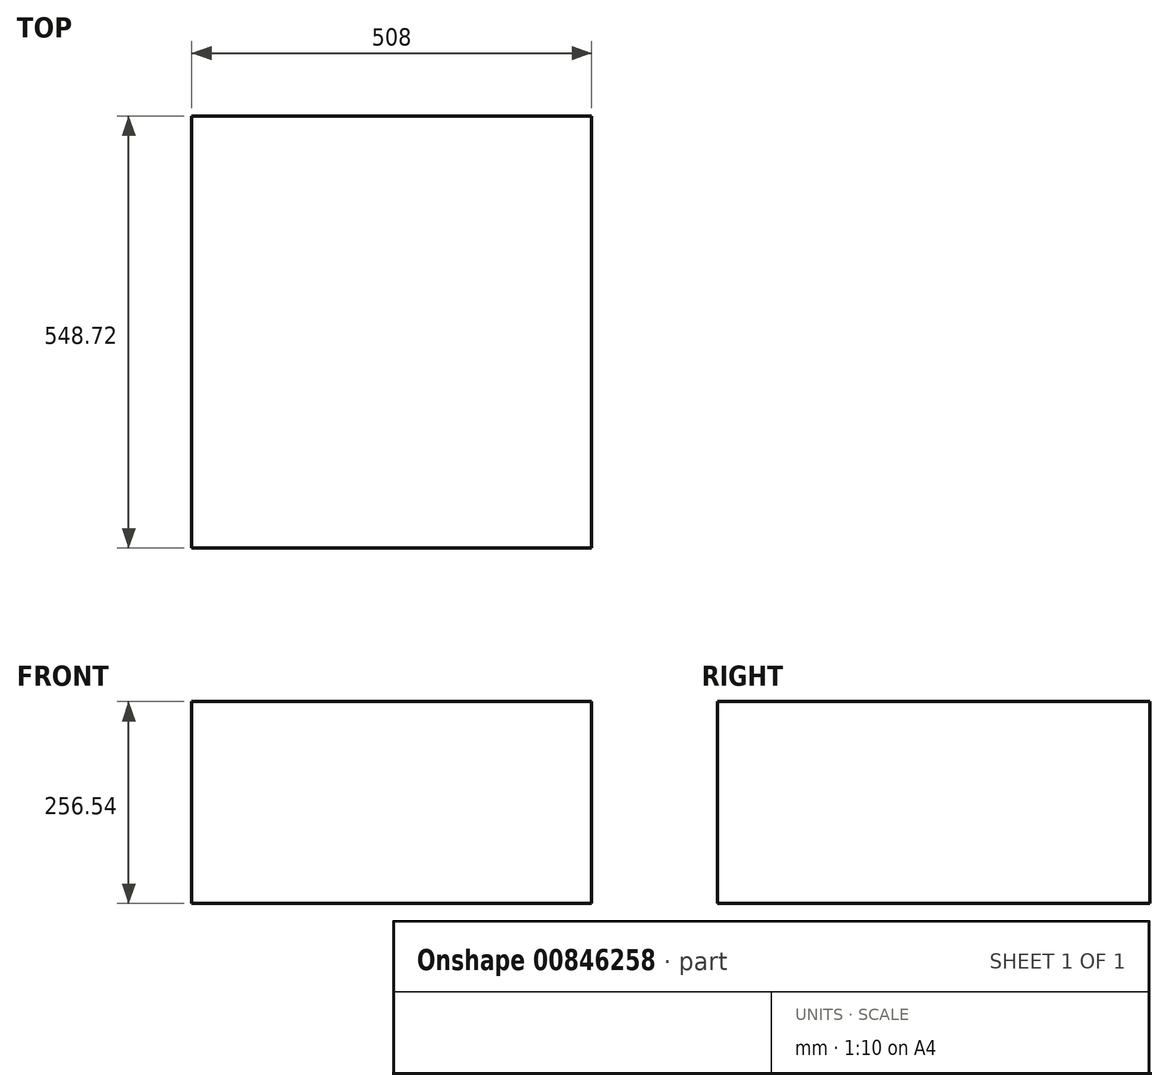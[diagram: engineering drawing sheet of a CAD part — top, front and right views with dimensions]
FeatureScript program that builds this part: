
annotation { "Feature Type Name" : "Feature", "Feature Type Description" : "" }
export const myFeature = defineFeature(function(context is Context, id is Id, definition is map)
    precondition{}
    {
        {
            var Q0;
            Q0=qCreatedBy(makeId("Top.planeOp"),FACE);
            var sketch = newSketch(context, id + "F0", { "sketchPlane" : qUnion([Q0])});
            skLineSegment(sketch, "E0.bottom", {"start": v(-260.11, 277.16) * mm, "end": v(247.89, 277.16) * mm});
            skLineSegment(sketch, "E0.top", {"start": v(-260.11, -271.56) * mm, "end": v(247.89, -271.56) * mm});
            skLineSegment(sketch, "E0.left", {"start": v(-260.11, 277.16) * mm, "end": v(-260.11, -271.56) * mm});
            skLineSegment(sketch, "E0.right", {"start": v(247.89, 277.16) * mm, "end": v(247.89, -271.56) * mm});
            skSolve(sketch);
        }
        {
            var Q0;
            Q0 = qSketchRegion(id + "F0", true);
            extrude(context, id + "F1", {"entities" : qUnion([Q0]), "depth" : 256.54 * mm, "offsetDistance" : 25.4 * mm});
        }
    });
